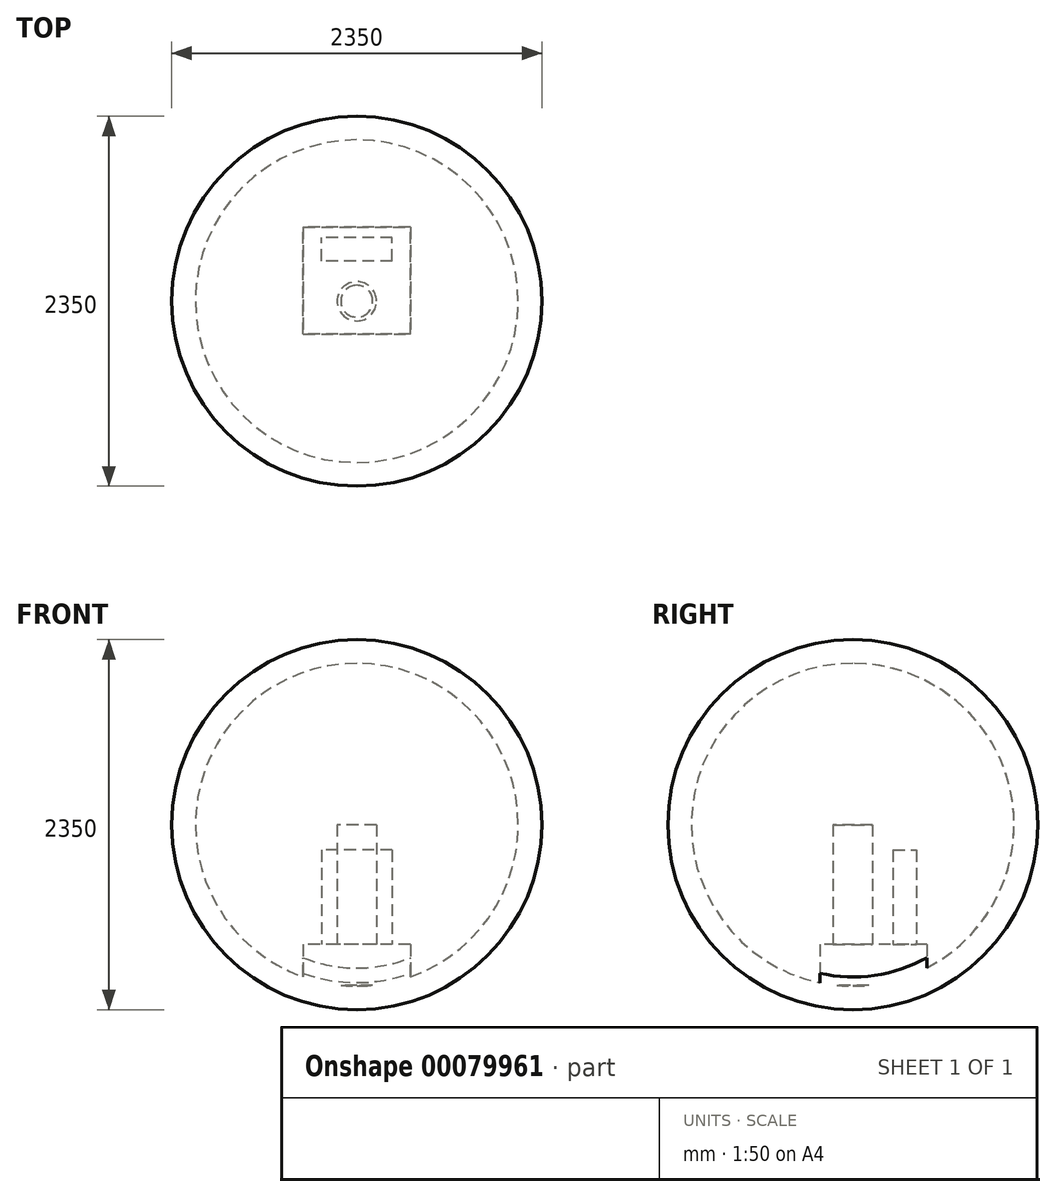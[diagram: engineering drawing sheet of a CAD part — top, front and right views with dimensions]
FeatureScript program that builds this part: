
annotation { "Feature Type Name" : "Feature", "Feature Type Description" : "" }
export const myFeature = defineFeature(function(context is Context, id is Id, definition is map)
    precondition{}
    {
        {
            var Q0;
            Q0=qCreatedBy(makeId("Top.planeOp"),FACE);
            var sketch = newSketch(context, id + "F0", { "sketchPlane" : qUnion([Q0])});
            skLineSegment(sketch, "E0.bottom", {"start": v(340, 340) * mm, "end": v(-340, 340) * mm});
            skLineSegment(sketch, "E0.top", {"start": v(340, -340) * mm, "end": v(-340, -340) * mm});
            skLineSegment(sketch, "E0.left", {"start": v(340, 340) * mm, "end": v(340, -340) * mm});
            skLineSegment(sketch, "E0.right", {"start": v(-340, 340) * mm, "end": v(-340, -340) * mm});
            skPoint(sketch, "E0.middle", {"position": v(0, 0) * mm});
            skSolve(sketch);
        }
        {
            var Q0;
            Q0 = qSketchRegion(id + "F0", true);
            extrude(context, id + "F1", {"entities" : qUnion([Q0]), "depth" : 260 * mm});
        }
        {
            var Q0;
            Q0=makeQuery(id+"F1.opExtrude","CAP_FACE",FACE,{"disambiguationData":[OSD([sQuery(id+"F0.wireOp",EDGE,"E0.bottom"),sQuery(id+"F0.wireOp",EDGE,"E0.top"),sQuery(id+"F0.wireOp",EDGE,"E0.left"),sQuery(id+"F0.wireOp",EDGE,"E0.right")])],"isStart":false});
            var sketch = newSketch(context, id + "F2", { "sketchPlane" : qUnion([Q0])});
            skCircle(sketch, "E1", {"center": v(0, -130) * mm, "radius": 125 * mm});
            skLineSegment(sketch, "E2.bottom", {"start": v(225, 125) * mm, "end": v(-225, 125) * mm});
            skLineSegment(sketch, "E2.top", {"start": v(225, 275) * mm, "end": v(-225, 275) * mm});
            skLineSegment(sketch, "E2.left", {"start": v(225, 125) * mm, "end": v(225, 275) * mm});
            skLineSegment(sketch, "E2.right", {"start": v(-225, 125) * mm, "end": v(-225, 275) * mm});
            skPoint(sketch, "E2.middle", {"position": v(0, 200) * mm});
            skSolve(sketch);
        }
        {
            var Q0;
            Q0=makeQuery(id+"F2.imprint","IMPRINT",FACE,{"disambiguationData":[TD([[makeQuery(id+"F2.imprint","IMPRINT",EDGE,{"derivedFrom":sQuery(id+"F2.wireOp",EDGE,"E1")}),1.0]])]});
            extrude(context, id + "F3", {"entities" : qUnion([Q0]), "operationType" : NewBodyOperationType.ADD, "depth" : 760 * mm});
        }
        {
            var Q0;
            Q0=makeQuery(id+"F2.imprint","IMPRINT",FACE,{"disambiguationData":[TD([[makeQuery(id+"F2.imprint","IMPRINT",EDGE,{"derivedFrom":sQuery(id+"F2.wireOp",EDGE,"E2.bottom")}),-1.0]])]});
            extrude(context, id + "F4", {"entities" : qUnion([Q0]), "operationType" : NewBodyOperationType.ADD, "depth" : 600 * mm});
        }
        {
            var Q0;
            Q0=qCreatedBy(makeId("Right.planeOp"),FACE);
            var sketch = newSketch(context, id + "F5", { "sketchPlane" : qUnion([Q0])});
            skLineSegment(sketch, "E3", {"start": v(-130, 2045) * mm, "end": v(-130, -5) * mm});
            skArc(sketch, "E4", {"start": v(-130, 2045) * mm, "mid": v(-1155, 1020) * mm, "end": v(-130, -5) * mm});
            skArc(sketch, "E5", {"start": v(-130, -155) * mm, "mid": v(1045, 1020) * mm, "end": v(-130, 2195) * mm});
            skLineSegment(sketch, "E6", {"start": v(-130, 2195) * mm, "end": v(-130, -155) * mm});
            skArc(sketch, "E7", {"start": v(-130, 125) * mm, "mid": v(765, 1020) * mm, "end": v(-130, 1915) * mm});
            skSolve(sketch);
        }
        {
            var Q0;
            {var subQ0=sQuery(id+"F5.wireOp",EDGE,"E7");Q0=makeQuery(id+"F5.imprint","IMPRINT",FACE,{"disambiguationData":[TD([[makeQuery(id+"F5.imprint","IMPRINT",EDGE,{"derivedFrom":subQ0}),1.0]])]});}
            var Q1;
            {var subQ5=sQuery(id+"F5.wireOp",EDGE,"E5");Q1=makeQuery(id+"F5.imprint","IMPRINT",FACE,{"disambiguationData":[TD([[makeQuery(id+"F5.imprint","IMPRINT",EDGE,{"derivedFrom":subQ5}),1.0]])]});}
            var Q2;
            {var subQ0=sQuery(id+"F5.wireOp",EDGE,"E4");Q2=makeQuery(id+"F5.imprint","IMPRINT",FACE,{"disambiguationData":[TD([[makeQuery(id+"F5.imprint","IMPRINT",EDGE,{"derivedFrom":subQ0}),1.0]])]});}
            var Q3;
            Q3=sQuery(id+"F5.wireOp",EDGE,"E6");
            revolve(context, id + "F6", {"operationType" : NewBodyOperationType.ADD, "entities" : qUnion([Q0, Q1, Q2]), "axis" : qUnion([Q3]), "revolveType" : RevolveType.FULL});
        }
    });
